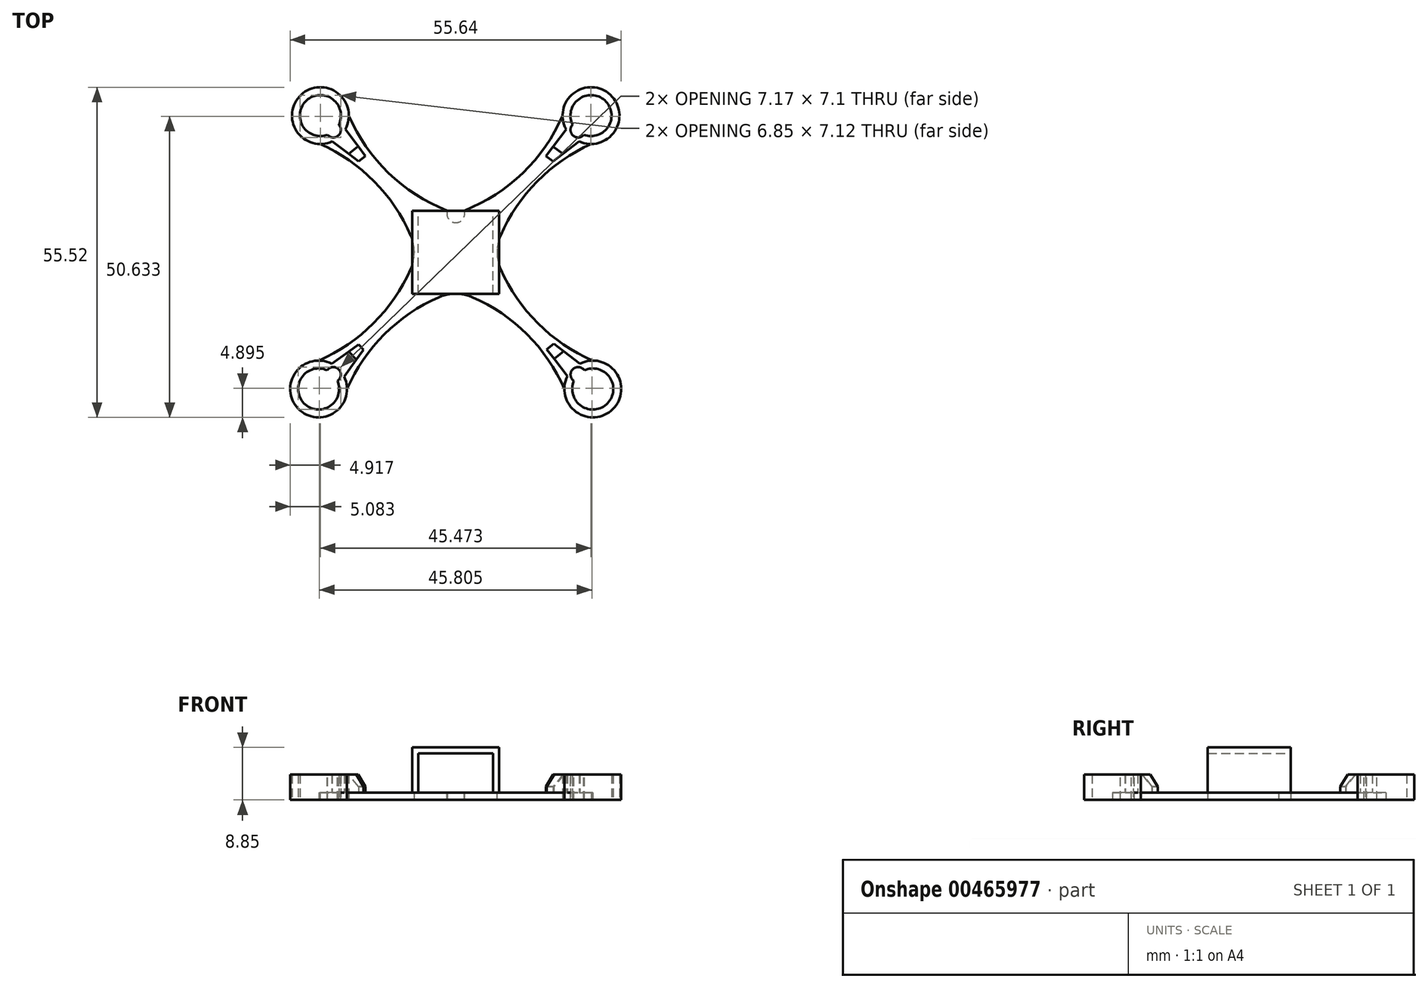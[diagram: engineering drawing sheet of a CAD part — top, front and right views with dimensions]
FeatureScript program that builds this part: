
annotation { "Feature Type Name" : "Feature", "Feature Type Description" : "" }
export const myFeature = defineFeature(function(context is Context, id is Id, definition is map)
    precondition{}
    {
        {
            var Q0;
            Q0=qCreatedBy(makeId("Top.planeOp"),FACE);
            var sketch = newSketch(context, id + "F0", { "sketchPlane" : qUnion([Q0])});
            skLineSegment(sketch, "E0.bottom", {"start": v(-22.75, 22.99) * mm, "end": v(22.75, 22.99) * mm, "construction": true});
            skLineSegment(sketch, "E0.top", {"start": v(-23.05, -22.99) * mm, "end": v(23.05, -22.99) * mm, "construction": true});
            skCircle(sketch, "E1", {"center": v(-22.75, 22.99) * mm, "radius": 3.45 * mm});
            skArc(sketch, "E2", {"start": v(-17.97, 22.99) * mm, "mid": v(-26.12, 26.37) * mm, "end": v(-22.78, 18.21) * mm});
            skArc(sketch, "E3", {"start": v(22.78, 18.21) * mm, "mid": v(26.12, 26.37) * mm, "end": v(17.98, 22.99) * mm});
            skCircle(sketch, "E4", {"center": v(22.75, 22.99) * mm, "radius": 3.45 * mm});
            skArc(sketch, "E5", {"start": v(18.27, -22.99) * mm, "mid": v(26.44, -26.35) * mm, "end": v(23.02, -18.21) * mm});
            skArc(sketch, "E6", {"start": v(-23.02, -18.21) * mm, "mid": v(-26.44, -26.35) * mm, "end": v(-18.27, -22.99) * mm});
            skCircle(sketch, "E7", {"center": v(-23.05, -22.99) * mm, "radius": 3.45 * mm});
            skCircle(sketch, "E8", {"center": v(23.05, -22.99) * mm, "radius": 3.45 * mm});
            skCircle(sketch, "E9", {"center": v(0, 0) * mm, "radius": 6.48 * mm, "construction": true});
            skArc(sketch, "E10", {"start": v(-17.97, 22.99) * mm, "mid": v(-10.74, 12.82) * mm, "end": v(0, 6.48) * mm});
            skArc(sketch, "E11", {"start": v(0, 6.48) * mm, "mid": v(10.74, 12.82) * mm, "end": v(17.98, 22.99) * mm});
            skArc(sketch, "E12", {"start": v(22.78, 18.21) * mm, "mid": v(12.7, 10.84) * mm, "end": v(6.48, 0) * mm});
            skArc(sketch, "E13", {"start": v(6.48, 0) * mm, "mid": v(12.8, -10.88) * mm, "end": v(23.02, -18.21) * mm});
            skArc(sketch, "E14", {"start": v(18.28, -22.99) * mm, "mid": v(10.9, -12.77) * mm, "end": v(0, -6.48) * mm});
            skArc(sketch, "E15", {"start": v(-23.02, -18.21) * mm, "mid": v(-12.8, -10.88) * mm, "end": v(-6.48, 0) * mm});
            skArc(sketch, "E16", {"start": v(0, -6.48) * mm, "mid": v(-10.9, -12.77) * mm, "end": v(-18.27, -22.99) * mm});
            skArc(sketch, "E17", {"start": v(-6.48, 0) * mm, "mid": v(-12.7, 10.84) * mm, "end": v(-22.78, 18.21) * mm});
            skLineSegment(sketch, "E18", {"start": v(0, 0) * mm, "end": v(0, 42) * mm, "construction": true});
            skLineSegment(sketch, "E19", {"start": v(-22.75, 22.99) * mm, "end": v(-23.05, -22.99) * mm, "construction": true});
            skLineSegment(sketch, "E20", {"start": v(22.75, 22.99) * mm, "end": v(23.05, -22.99) * mm, "construction": true});
            skPoint(sketch, "E21", {"position": v(-27.06, -20.4) * mm});
            skPoint(sketch, "E22", {"position": v(27.82, -23.02) * mm});
            skSolve(sketch);
        }
        {
            var Q0;
            Q0 = qSketchRegion(id + "F0", true);
            var Q1;
            Q1 = qConstructionFilter(qBodyType(qCreatedBy(id + "F0" ,EDGE), BodyType.WIRE), ConstructionObject.NO);
            extrude(context, id + "F1", {"entities" : qUnion([Q0]), "surfaceEntities" : qUnion([Q1]), "depth" : 1.25 * mm});
        }
        {
            var Q0;
            Q0=makeQuery(id+"F1.opExtrude","CAP_FACE",FACE,{"disambiguationData":[OSD([sQuery(id+"F0.wireOp",EDGE,"E1"),sQuery(id+"F0.wireOp",EDGE,"E2"),sQuery(id+"F0.wireOp",EDGE,"E3"),sQuery(id+"F0.wireOp",EDGE,"E4"),sQuery(id+"F0.wireOp",EDGE,"E5"),sQuery(id+"F0.wireOp",EDGE,"E6"),sQuery(id+"F0.wireOp",EDGE,"E7"),sQuery(id+"F0.wireOp",EDGE,"E8"),sQuery(id+"F0.wireOp",EDGE,"E10"),sQuery(id+"F0.wireOp",EDGE,"E11"),sQuery(id+"F0.wireOp",EDGE,"E12"),sQuery(id+"F0.wireOp",EDGE,"E13"),sQuery(id+"F0.wireOp",EDGE,"E14"),sQuery(id+"F0.wireOp",EDGE,"E15"),sQuery(id+"F0.wireOp",EDGE,"E16"),sQuery(id+"F0.wireOp",EDGE,"E17")])],"isStart":false});
            var sketch = newSketch(context, id + "F2", { "sketchPlane" : qUnion([Q0])});
            skCircle(sketch, "E23", {"center": v(-20.58, 20.58) * mm, "radius": 1.27 * mm});
            skCircle(sketch, "E24", {"center": v(20.58, 20.58) * mm, "radius": 1.27 * mm});
            skCircle(sketch, "E25", {"center": v(20.58, -20.58) * mm, "radius": 1.27 * mm});
            skCircle(sketch, "E26", {"center": v(-20.58, -20.58) * mm, "radius": 1.27 * mm});
            skLineSegment(sketch, "E27", {"start": v(-20.58, 20.58) * mm, "end": v(20.58, -20.58) * mm, "construction": true});
            skLineSegment(sketch, "E28", {"start": v(20.58, 20.58) * mm, "end": v(-20.58, -20.58) * mm, "construction": true});
            skPoint(sketch, "E29", {"position": v(0, 0) * mm});
            skSolve(sketch);
        }
        {
            var Q0;
            Q0 = qSketchRegion(id + "F2", true);
            extrude(context, id + "F3", {"entities" : qUnion([Q0]), "operationType" : NewBodyOperationType.REMOVE, "oppositeDirection" : true, "depth" : 15.24 * mm});
        }
        {
            var Q0;
            Q0=qCreatedBy(makeId("Front.planeOp"),FACE);
            var sketch = newSketch(context, id + "F4", { "sketchPlane" : qUnion([Q0])});
            skLineSegment(sketch, "E30.bottom", {"start": v(-6.3, 7.85) * mm, "end": v(6.3, 7.85) * mm});
            skLineSegment(sketch, "E30.left", {"start": v(-6.3, 7.85) * mm, "end": v(-6.3, 1.25) * mm});
            skLineSegment(sketch, "E30.right", {"start": v(6.3, 7.85) * mm, "end": v(6.3, 1.25) * mm});
            skLineSegment(sketch, "E31.0", {"start": v(-7.3, 8.85) * mm, "end": v(-7.3, 1.25) * mm});
            skLineSegment(sketch, "E31.1", {"start": v(-7.3, 8.85) * mm, "end": v(7.3, 8.85) * mm});
            skLineSegment(sketch, "E31.2", {"start": v(7.3, 8.85) * mm, "end": v(7.3, 1.25) * mm});
            skLineSegment(sketch, "E32", {"start": v(-7.3, 1.25) * mm, "end": v(-6.3, 1.25) * mm});
            skLineSegment(sketch, "E33", {"start": v(6.3, 1.25) * mm, "end": v(7.3, 1.25) * mm});
            skSolve(sketch);
        }
        {
            var Q0;
            Q0 = qSketchRegion(id + "F4", true);
            extrude(context, id + "F5", {"entities" : qUnion([Q0]), "operationType" : NewBodyOperationType.ADD, "endBound" : BoundingType.SYMMETRIC, "depth" : 14 * mm});
        }
        {
            var Q0;
            Q0=makeQuery(id+"F1.opExtrude","CAP_FACE",FACE,{"disambiguationData":[OSD([sQuery(id+"F0.wireOp",EDGE,"E1"),sQuery(id+"F0.wireOp",EDGE,"E2"),sQuery(id+"F0.wireOp",EDGE,"E3"),sQuery(id+"F0.wireOp",EDGE,"E4"),sQuery(id+"F0.wireOp",EDGE,"E5"),sQuery(id+"F0.wireOp",EDGE,"E6"),sQuery(id+"F0.wireOp",EDGE,"E7"),sQuery(id+"F0.wireOp",EDGE,"E8"),sQuery(id+"F0.wireOp",EDGE,"E10"),sQuery(id+"F0.wireOp",EDGE,"E11"),sQuery(id+"F0.wireOp",EDGE,"E12"),sQuery(id+"F0.wireOp",EDGE,"E13"),sQuery(id+"F0.wireOp",EDGE,"E14"),sQuery(id+"F0.wireOp",EDGE,"E15"),sQuery(id+"F0.wireOp",EDGE,"E16"),sQuery(id+"F0.wireOp",EDGE,"E17")])],"isStart":false});
            var sketch = newSketch(context, id + "F6", { "sketchPlane" : qUnion([Q0])});
            skCircle(sketch, "E34", {"center": v(0, 6.48) * mm, "radius": 1.5 * mm});
            skSolve(sketch);
        }
        {
            var Q0;
            Q0 = qSketchRegion(id + "F6", true);
            extrude(context, id + "F7", {"entities" : qUnion([Q0]), "operationType" : NewBodyOperationType.REMOVE, "endBound" : BoundingType.UP_TO_NEXT, "oppositeDirection" : true, "depth" : 25 * mm});
        }
        {
            var Q0;
            Q0=makeQuery(id+"F1.opExtrude","CAP_FACE",FACE,{"disambiguationData":[OSD([sQuery(id+"F0.wireOp",EDGE,"E1"),sQuery(id+"F0.wireOp",EDGE,"E2"),sQuery(id+"F0.wireOp",EDGE,"E3"),sQuery(id+"F0.wireOp",EDGE,"E4"),sQuery(id+"F0.wireOp",EDGE,"E5"),sQuery(id+"F0.wireOp",EDGE,"E6"),sQuery(id+"F0.wireOp",EDGE,"E7"),sQuery(id+"F0.wireOp",EDGE,"E8"),sQuery(id+"F0.wireOp",EDGE,"E10"),sQuery(id+"F0.wireOp",EDGE,"E11"),sQuery(id+"F0.wireOp",EDGE,"E12"),sQuery(id+"F0.wireOp",EDGE,"E13"),sQuery(id+"F0.wireOp",EDGE,"E14"),sQuery(id+"F0.wireOp",EDGE,"E15"),sQuery(id+"F0.wireOp",EDGE,"E16"),sQuery(id+"F0.wireOp",EDGE,"E17")])],"isStart":false});
            var sketch = newSketch(context, id + "F8", { "sketchPlane" : qUnion([Q0])});
            skArc(sketch, "E35.0", {"start": v(-19.66, 21.45) * mm, "mid": v(-25.06, 25.55) * mm, "end": v(-21.54, 19.75) * mm});
            skArc(sketch, "E35.1", {"start": v(-21.54, 19.75) * mm, "mid": v(-19.73, 19.64) * mm, "end": v(-19.66, 21.45) * mm});
            skArc(sketch, "E35.2", {"start": v(21.54, 19.75) * mm, "mid": v(25.06, 25.55) * mm, "end": v(19.66, 21.45) * mm});
            skArc(sketch, "E35.3", {"start": v(19.66, 21.45) * mm, "mid": v(19.73, 19.64) * mm, "end": v(21.54, 19.75) * mm});
            skArc(sketch, "E35.4", {"start": v(19.88, -21.64) * mm, "mid": v(25.52, -25.4) * mm, "end": v(21.62, -19.85) * mm});
            skArc(sketch, "E35.5", {"start": v(21.62, -19.85) * mm, "mid": v(19.67, -19.7) * mm, "end": v(19.88, -21.64) * mm});
            skArc(sketch, "E35.6", {"start": v(-21.62, -19.85) * mm, "mid": v(-25.52, -25.4) * mm, "end": v(-19.88, -21.64) * mm});
            skArc(sketch, "E36.converted", {"start": v(-20.85, -18.75) * mm, "mid": v(-26.47, -26.32) * mm, "end": v(-18.76, -20.9) * mm});
            skPoint(sketch, "E37.orphan", {"position": v(-18.27, -22.99) * mm});
            skArc(sketch, "E38.converted", {"start": v(-19.8, 19.24) * mm, "mid": v(-19.56, 19.43) * mm, "end": v(-19.34, 19.65) * mm});
            skPoint(sketch, "E39.orphan", {"position": v(-22.78, 18.21) * mm});
            skArc(sketch, "E40.converted", {"start": v(18.78, -20.84) * mm, "mid": v(26.43, -26.36) * mm, "end": v(20.9, -18.72) * mm});
            skPoint(sketch, "E41.orphan", {"position": v(23.02, -18.21) * mm});
            skArc(sketch, "E42.converted", {"start": v(20.77, 18.64) * mm, "mid": v(26, 26.49) * mm, "end": v(18.57, 20.68) * mm});
            skPoint(sketch, "E43.orphan", {"position": v(22.78, 18.21) * mm});
            skArc(sketch, "E44.4", {"start": v(-19.88, -21.64) * mm, "mid": v(-19.67, -19.7) * mm, "end": v(-21.62, -19.85) * mm});
            skPoint(sketch, "E45.startSnap0", {"position": v(-19.67, -19.7) * mm});
            skPoint(sketch, "E45.endSnap0", {"position": v(-46.08, 20.5) * mm});
            skLineSegment(sketch, "E46", {"start": v(-16.36, -15.53) * mm, "end": v(-15.51, -16.38) * mm});
            skLineSegment(sketch, "E47", {"start": v(-15.51, -16.38) * mm, "end": v(-18.76, -20.9) * mm});
            skLineSegment(sketch, "E48", {"start": v(-16.36, -15.53) * mm, "end": v(-20.85, -18.75) * mm});
            skLineSegment(sketch, "E49", {"start": v(-19.67, -19.7) * mm, "end": v(-15.94, -15.96) * mm, "construction": true});
            skLineSegment(sketch, "E50", {"start": v(-20.77, 18.64) * mm, "end": v(-16.35, 15.3) * mm});
            skLineSegment(sketch, "E51", {"start": v(-16.35, 15.3) * mm, "end": v(-15.16, 16.21) * mm});
            skLineSegment(sketch, "E52", {"start": v(-15.16, 16.21) * mm, "end": v(-18.57, 20.68) * mm});
            skLineSegment(sketch, "E53", {"start": v(-20.58, 20.58) * mm, "end": v(-15.76, 15.76) * mm, "construction": true});
            skLineSegment(sketch, "E54", {"start": v(-22.75, 22.99) * mm, "end": v(-20.58, 20.58) * mm, "construction": true});
            skLineSegment(sketch, "E55", {"start": v(-21.66, 21.78) * mm, "end": v(-17.97, 18.1) * mm});
            skArc(sketch, "E56.trimOffspring", {"start": v(-18.57, 20.68) * mm, "mid": v(-26, 26.49) * mm, "end": v(-20.77, 18.64) * mm});
            skLineSegment(sketch, "E57", {"start": v(18.57, 20.68) * mm, "end": v(15.15, 16.2) * mm});
            skLineSegment(sketch, "E58", {"start": v(15.15, 16.2) * mm, "end": v(16.35, 15.3) * mm});
            skLineSegment(sketch, "E59", {"start": v(16.35, 15.3) * mm, "end": v(20.77, 18.64) * mm});
            skLineSegment(sketch, "E60", {"start": v(20.58, 20.58) * mm, "end": v(15.75, 15.75) * mm, "construction": true});
            skLineSegment(sketch, "E61", {"start": v(18.78, -20.84) * mm, "end": v(15.32, -16.3) * mm});
            skLineSegment(sketch, "E62", {"start": v(15.32, -16.3) * mm, "end": v(16.51, -15.4) * mm});
            skLineSegment(sketch, "E63", {"start": v(16.51, -15.4) * mm, "end": v(20.9, -18.72) * mm});
            skLineSegment(sketch, "E64", {"start": v(15.92, -15.85) * mm, "end": v(23.05, -22.99) * mm, "construction": true});
            skSolve(sketch);
        }
        {
            var Q0;
            Q0 = qSketchRegion(id + "F8", true);
            extrude(context, id + "F9", {"entities" : qUnion([Q0]), "operationType" : NewBodyOperationType.ADD, "depth" : 3 * mm});
        }
        {
            var Q0;
            Q0=makeQuery(id+"F9.opExtrude","CAP_EDGE",EDGE,{"disambiguationData":[OSD([sQuery(id+"F8.wireOp",EDGE,"E51")])],"isStart":false});
            var Q1;
            Q1=makeQuery(id+"F9.opExtrude","CAP_EDGE",EDGE,{"disambiguationData":[OSD([sQuery(id+"F8.wireOp",EDGE,"E46")])],"isStart":false});
            var Q2;
            Q2=makeQuery(id+"F9.opExtrude","CAP_EDGE",EDGE,{"disambiguationData":[OSD([sQuery(id+"F8.wireOp",EDGE,"E62")])],"isStart":false});
            var Q3;
            Q3=makeQuery(id+"F9.opExtrude","CAP_EDGE",EDGE,{"disambiguationData":[OSD([sQuery(id+"F8.wireOp",EDGE,"E58")])],"isStart":false});
            chamfer(context, id + "F10", {"entities" : qUnion([Q0, Q1, Q2, Q3]), "width" : 2 * mm, "tangentPropagation" : true});
        }
        {
            var Q0;
            Q0=makeQuery(id+"F1.opExtrude","SWEPT_EDGE",EDGE,{"disambiguationData":[OSD([sQuery(id+"F0.wireOp",EDGE,"E15"),sQuery(id+"F0.wireOp",EDGE,"E17")])]});
            var Q1;
            Q1=makeQuery(id+"F1.opExtrude","SWEPT_EDGE",EDGE,{"disambiguationData":[OSD([sQuery(id+"F0.wireOp",EDGE,"E14"),sQuery(id+"F0.wireOp",EDGE,"E16")])]});
            var Q2;
            Q2=makeQuery(id+"F1.opExtrude","SWEPT_EDGE",EDGE,{"disambiguationData":[OSD([sQuery(id+"F0.wireOp",EDGE,"E12"),sQuery(id+"F0.wireOp",EDGE,"E13")])]});
            fillet(context, id + "F11", {"entities" : qUnion([Q0, Q1, Q2]), "radius" : 7 * mm, "tangentPropagation" : true, "allowEdgeOverflow" : false});
        }
    });
